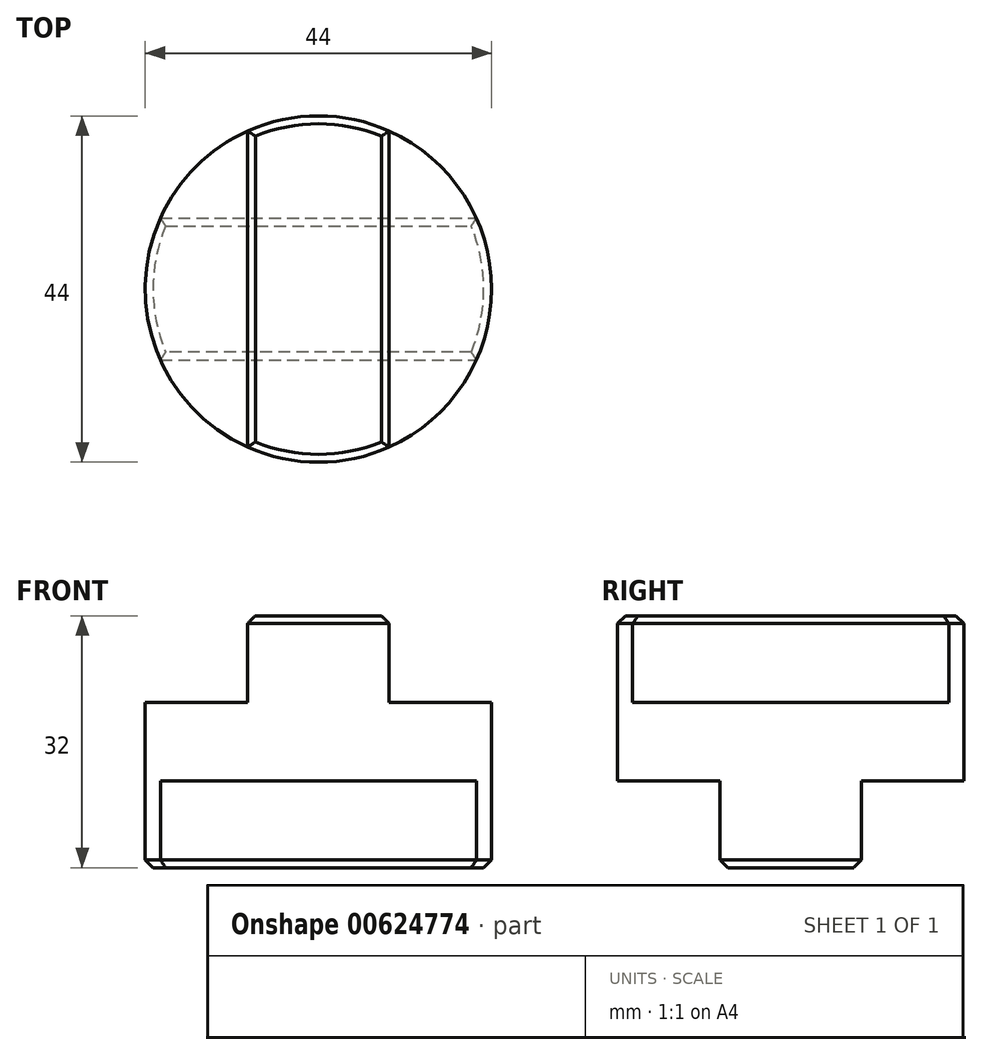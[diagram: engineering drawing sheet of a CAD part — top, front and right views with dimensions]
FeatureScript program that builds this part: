
annotation { "Feature Type Name" : "Feature", "Feature Type Description" : "" }
export const myFeature = defineFeature(function(context is Context, id is Id, definition is map)
    precondition{}
    {
        {
            var Q0;
            Q0=qCreatedBy(makeId("Top.planeOp"),FACE);
            var sketch = newSketch(context, id + "F0", { "sketchPlane" : qUnion([Q0])});
            skCircle(sketch, "E0", {"center": v(0, 0) * mm, "radius": 22 * mm});
            skSolve(sketch);
        }
        {
            var Q0;
            Q0 = qSketchRegion(id + "F0", true);
            extrude(context, id + "F1", {"entities" : qUnion([Q0]), "depth" : 32 * mm, "offsetDistance" : 25 * mm});
        }
        {
            var Q0;
            Q0=qCreatedBy(makeId("Front.planeOp"),FACE);
            var sketch = newSketch(context, id + "F2", { "sketchPlane" : qUnion([Q0])});
            skPoint(sketch, "E1.middle", {"position": v(0, 0) * mm});
            skLineSegment(sketch, "E2.bottom", {"start": v(-9, 21) * mm, "end": v(-23.37, 21) * mm});
            skLineSegment(sketch, "E2.top", {"start": v(-9, 33.76) * mm, "end": v(-23.37, 33.76) * mm});
            skLineSegment(sketch, "E2.left", {"start": v(-9, 21) * mm, "end": v(-9, 33.76) * mm});
            skLineSegment(sketch, "E2.right", {"start": v(-23.37, 21) * mm, "end": v(-23.37, 33.76) * mm});
            skLineSegment(sketch, "E3.bottom", {"start": v(9, 21) * mm, "end": v(22.82, 21) * mm});
            skLineSegment(sketch, "E3.top", {"start": v(9, 32.85) * mm, "end": v(22.82, 32.85) * mm});
            skLineSegment(sketch, "E3.left", {"start": v(9, 21) * mm, "end": v(9, 32.85) * mm});
            skLineSegment(sketch, "E3.right", {"start": v(22.82, 21) * mm, "end": v(22.82, 32.85) * mm});
            skPoint(sketch, "E1.top.end.orphan", {"position": v(9, -21) * mm});
            skPoint(sketch, "E1.left.end.orphan", {"position": v(-9, -21) * mm});
            skSolve(sketch);
        }
        {
            var Q0;
            Q0 = qSketchRegion(id + "F2", true);
            extrude(context, id + "F3", {"entities" : qUnion([Q0]), "operationType" : NewBodyOperationType.REMOVE, "endBound" : BoundingType.THROUGH_ALL, "depth" : 25 * mm, "offsetDistance" : 25 * mm, "hasSecondDirection" : true, "secondDirectionOppositeDirection" : true, "secondDirectionDepth" : 25 * mm});
        }
        {
            var Q0;
            Q0=qCreatedBy(makeId("Right.planeOp"),FACE);
            var sketch = newSketch(context, id + "F4", { "sketchPlane" : qUnion([Q0])});
            skLineSegment(sketch, "E4.left", {"start": v(-9, 11) * mm, "end": v(-9, -4.1) * mm});
            skLineSegment(sketch, "E4.right", {"start": v(9, 11) * mm, "end": v(9, -1.2) * mm});
            skPoint(sketch, "E4.middle", {"position": v(0, 0) * mm});
            skLineSegment(sketch, "E5.bottom", {"start": v(-9, 11) * mm, "end": v(-25.21, 11) * mm});
            skLineSegment(sketch, "E5.top", {"start": v(-9, -4.1) * mm, "end": v(-25.21, -4.1) * mm});
            skLineSegment(sketch, "E5.right", {"start": v(-25.21, 11) * mm, "end": v(-25.21, -4.1) * mm});
            skLineSegment(sketch, "E6.bottom", {"start": v(9, 11) * mm, "end": v(25.44, 11) * mm});
            skLineSegment(sketch, "E6.top", {"start": v(9, -1.2) * mm, "end": v(25.44, -1.2) * mm});
            skLineSegment(sketch, "E6.right", {"start": v(25.44, 11) * mm, "end": v(25.44, -1.2) * mm});
            skPoint(sketch, "E7.orphan", {"position": v(9, -11) * mm});
            skPoint(sketch, "E8.orphan", {"position": v(-9, -11) * mm});
            skSolve(sketch);
        }
        {
            var Q0;
            Q0 = qSketchRegion(id + "F4", true);
            extrude(context, id + "F5", {"entities" : qUnion([Q0]), "operationType" : NewBodyOperationType.REMOVE, "endBound" : BoundingType.THROUGH_ALL, "oppositeDirection" : true, "depth" : 25 * mm, "offsetDistance" : 25 * mm, "hasSecondDirection" : true, "secondDirectionOppositeDirection" : false, "secondDirectionDepth" : 25 * mm});
        }
        {
            var Q0;
            Q0=makeQuery(id+"F1.opExtrude","CAP_FACE",FACE,{"disambiguationData":[OSD([sQuery(id+"F0.wireOp",EDGE,"E0")])],"isStart":false});
            var Q1;
            Q1=makeQuery(id+"F1.opExtrude","CAP_FACE",FACE,{"disambiguationData":[OSD([sQuery(id+"F0.wireOp",EDGE,"E0")])],"isStart":true});
            chamfer(context, id + "F6", {"entities" : qUnion([Q0, Q1]), "width" : 1 * mm, "tangentPropagation" : true});
        }
    });
